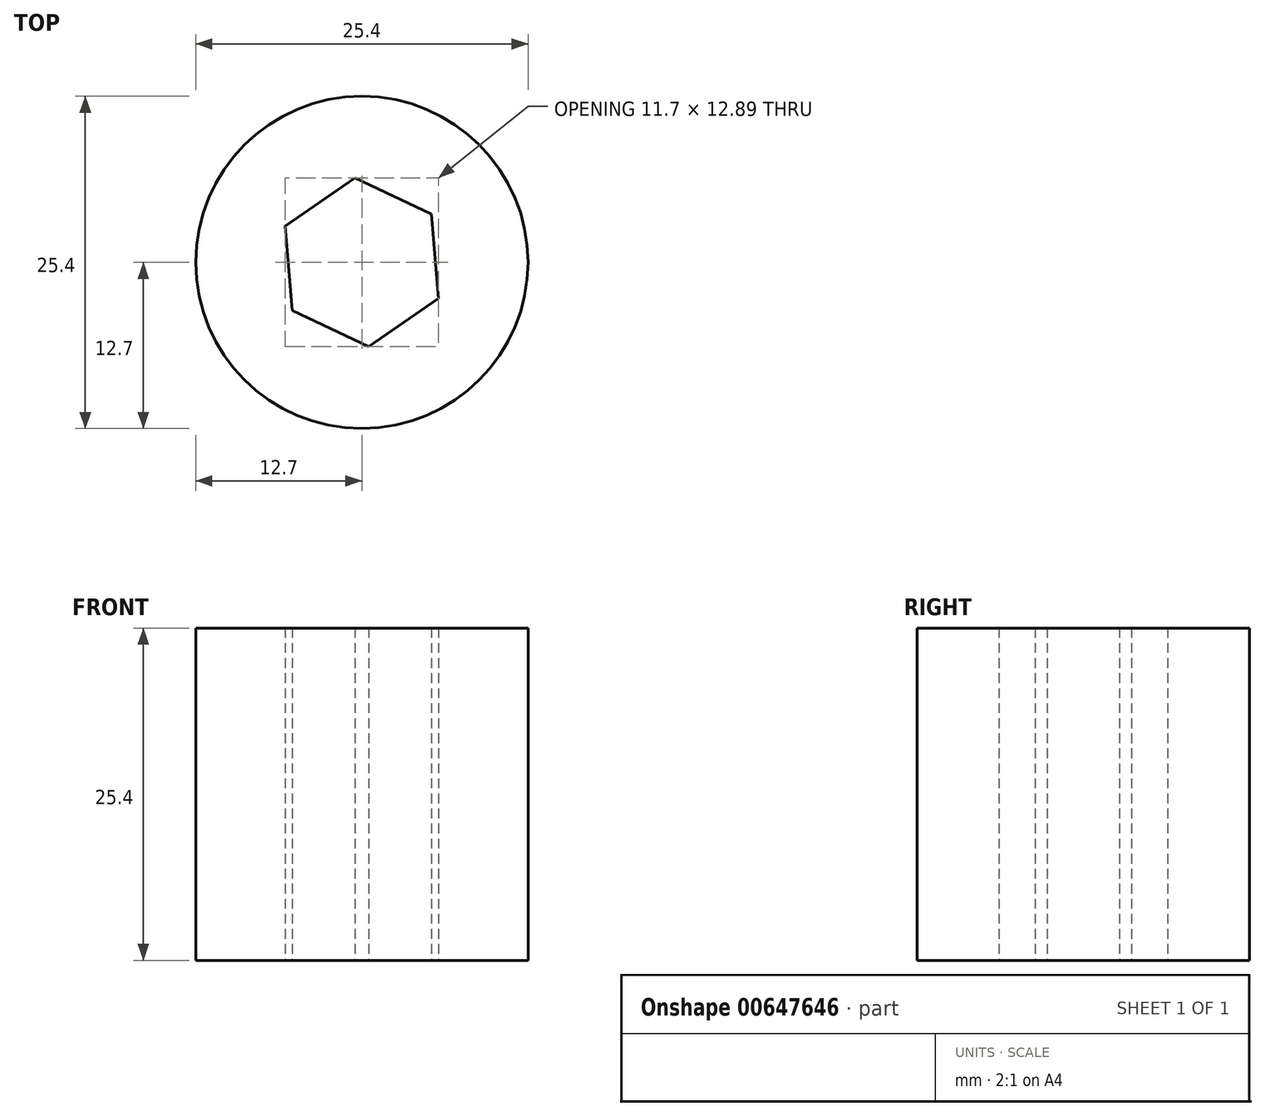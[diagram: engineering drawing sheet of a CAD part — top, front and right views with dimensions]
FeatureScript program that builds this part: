
annotation { "Feature Type Name" : "Feature", "Feature Type Description" : "" }
export const myFeature = defineFeature(function(context is Context, id is Id, definition is map)
    precondition{}
    {
        {
            var Q0;
            Q0=qCreatedBy(makeId("Top.planeOp"),FACE);
            var sketch = newSketch(context, id + "F0", { "sketchPlane" : qUnion([Q0])});
            skCircle(sketch, "E0", {"center": v(0, 0) * mm, "radius": 12.7 * mm});
            skCircle(sketch, "E1.cCircle", {"center": v(0, 0) * mm, "radius": 5.6 * mm, "construction": true});
            skLineSegment(sketch, "E1.0", {"start": v(5.31, 3.68) * mm, "end": v(5.85, -2.76) * mm});
            skLineSegment(sketch, "E1.1", {"start": v(5.85, -2.76) * mm, "end": v(0.53, -6.44) * mm});
            skLineSegment(sketch, "E1.2", {"start": v(0.53, -6.44) * mm, "end": v(-5.31, -3.68) * mm});
            skLineSegment(sketch, "E1.3", {"start": v(-5.31, -3.68) * mm, "end": v(-5.85, 2.76) * mm});
            skLineSegment(sketch, "E1.4", {"start": v(-5.85, 2.76) * mm, "end": v(-0.53, 6.44) * mm});
            skLineSegment(sketch, "E1.5", {"start": v(-0.53, 6.44) * mm, "end": v(5.31, 3.68) * mm});
            skPoint(sketch, "E1.0.midPoint", {"position": v(5.58, 0.46) * mm});
            skSolve(sketch);
        }
        {
            var Q0;
            Q0=makeQuery(id+"F0.imprint","IMPRINT",FACE,{"disambiguationData":[TD([[makeQuery(id+"F0.imprint","IMPRINT",EDGE,{"derivedFrom":sQuery(id+"F0.wireOp",EDGE,"E0")}),1.0]])]});
            extrude(context, id + "F1", {"entities" : qUnion([Q0]), "depth" : 25.4 * mm, "offsetDistance" : 25 * mm});
        }
    });
